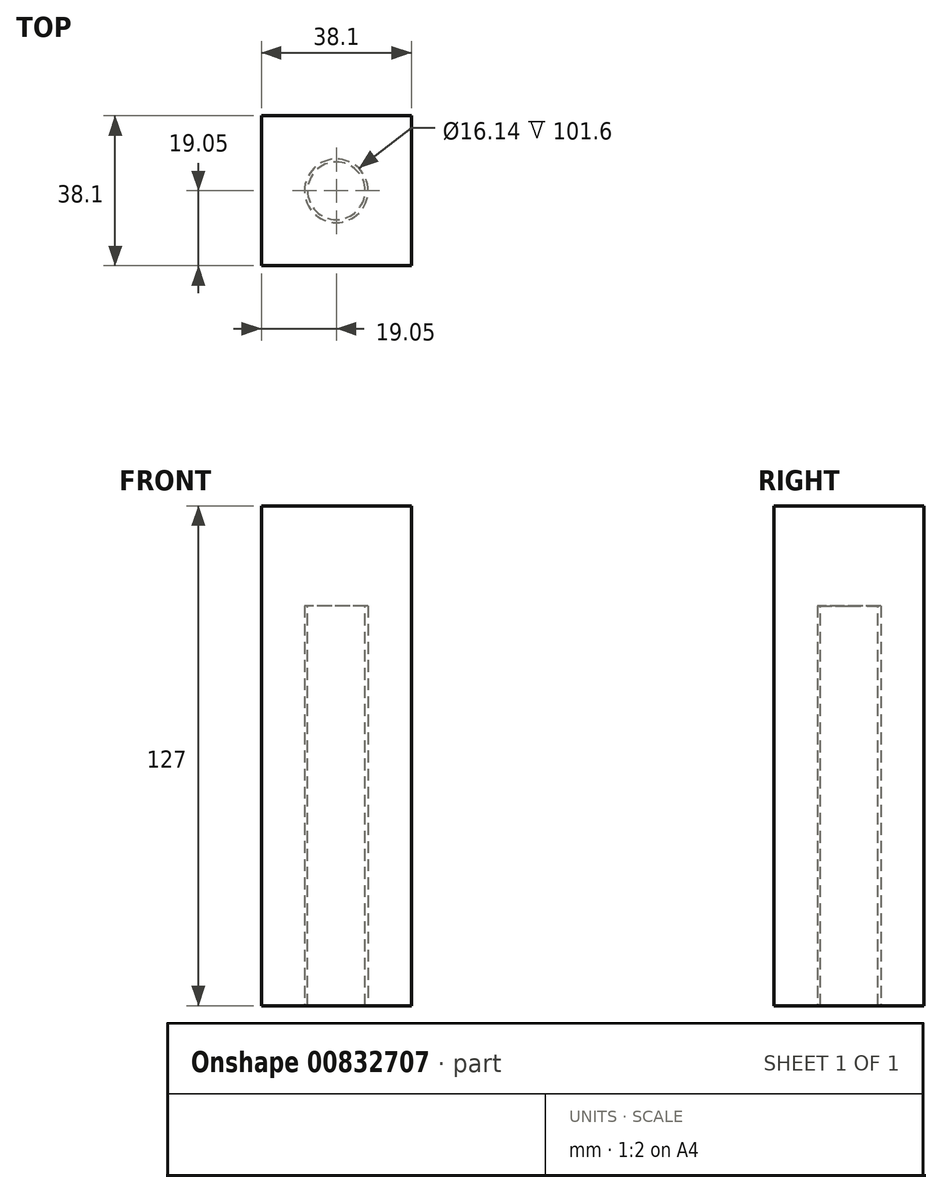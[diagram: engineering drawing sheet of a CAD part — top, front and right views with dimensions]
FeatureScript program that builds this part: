
annotation { "Feature Type Name" : "Feature", "Feature Type Description" : "" }
export const myFeature = defineFeature(function(context is Context, id is Id, definition is map)
    precondition{}
    {
        {
            var Q0;
            Q0=qCreatedBy(makeId("Top.planeOp"),FACE);
            var sketch = newSketch(context, id + "F0", { "sketchPlane" : qUnion([Q0])});
            skLineSegment(sketch, "E0", {"start": v(0, 0) * mm, "end": v(38.1, 0) * mm});
            skLineSegment(sketch, "E1", {"start": v(38.1, 0) * mm, "end": v(38.1, 38.1) * mm});
            skLineSegment(sketch, "E2", {"start": v(38.1, 38.1) * mm, "end": v(0, 38.1) * mm});
            skLineSegment(sketch, "E3", {"start": v(0, 38.1) * mm, "end": v(0, 0) * mm});
            skCircle(sketch, "E4", {"center": v(19.05, 19.05) * mm, "radius": 14.39 * mm});
            skPoint(sketch, "E4.centerSnap0", {"position": v(19.05, 38.1) * mm});
            skPoint(sketch, "E4.centerSnap1", {"position": v(0, 19.05) * mm});
            skCircle(sketch, "E5", {"center": v(19.05, 19.05) * mm, "radius": 8.07 * mm});
            skLineSegment(sketch, "E6", {"start": v(19.05, 0) * mm, "end": v(19.05, 38.1) * mm});
            skLineSegment(sketch, "E7", {"start": v(38.1, 19.05) * mm, "end": v(0, 19.05) * mm});
            skSolve(sketch);
        }
        {
            var Q0;
            {var subQ5=sQuery(id+"F0.wireOp",EDGE,"E2");var subQ7=sQuery(id+"F0.wireOp",EDGE,"E3");var subQ8=makeQuery(id+"F0.imprint","INTERSECT",VERTEX,{"derivedFrom":[subQ5,subQ7]});Q0=makeQuery(id+"F0.imprint","IMPRINT",FACE,{"disambiguationData":[TD([[makeQuery(id+"F0.imprint","IMPRINT",EDGE,{"disambiguationData":[TD([[subQ8,1.0]])],"derivedFrom":subQ5}),1.0]])]});}
            extrude(context, id + "F1", {"entities" : qUnion([Q0]), "depth" : 25.4 * mm, "offsetDistance" : 25.4 * mm});
        }
        {
            var Q0;
            {var subQ1=sQuery(id+"F0.wireOp",EDGE,"E2");var subQ5=sQuery(id+"F0.wireOp",EDGE,"E1");var subQ6=makeQuery(id+"F0.imprint","INTERSECT",VERTEX,{"derivedFrom":[subQ5,subQ1]});Q0=makeQuery(id+"F0.imprint","IMPRINT",FACE,{"disambiguationData":[TD([[makeQuery(id+"F0.imprint","IMPRINT",EDGE,{"disambiguationData":[TD([[subQ6,1.0]])],"derivedFrom":subQ5}),1.0]])]});}
            extrude(context, id + "F2", {"entities" : qUnion([Q0]), "operationType" : NewBodyOperationType.ADD, "depth" : 38.1 * mm, "offsetDistance" : 25.4 * mm});
        }
        {
            var Q0;
            {var subQ0=sQuery(id+"F0.wireOp",EDGE,"E1");var subQ1=sQuery(id+"F0.wireOp",EDGE,"E0");var subQ2=makeQuery(id+"F0.imprint","INTERSECT",VERTEX,{"derivedFrom":[subQ1,subQ0]});Q0=makeQuery(id+"F0.imprint","IMPRINT",FACE,{"disambiguationData":[TD([[makeQuery(id+"F0.imprint","IMPRINT",EDGE,{"disambiguationData":[TD([[subQ2,1.0]])],"derivedFrom":subQ1}),1.0]])]});}
            extrude(context, id + "F3", {"entities" : qUnion([Q0]), "operationType" : NewBodyOperationType.ADD, "depth" : 50.8 * mm, "offsetDistance" : 25.4 * mm});
        }
        {
            var Q0;
            {var subQ1=sQuery(id+"F0.wireOp",EDGE,"E0");var subQ6=sQuery(id+"F0.wireOp",EDGE,"E3");var subQ9=makeQuery(id+"F0.imprint","INTERSECT",VERTEX,{"derivedFrom":[subQ1,subQ6]});Q0=makeQuery(id+"F0.imprint","IMPRINT",FACE,{"disambiguationData":[TD([[makeQuery(id+"F0.imprint","IMPRINT",EDGE,{"disambiguationData":[TD([[subQ9,-1.0]])],"derivedFrom":subQ1}),1.0]])]});}
            extrude(context, id + "F4", {"entities" : qUnion([Q0]), "operationType" : NewBodyOperationType.ADD, "depth" : 63.5 * mm, "offsetDistance" : 25.4 * mm});
        }
        {
            var Q0;
            {var subQ0=sQuery(id+"F0.wireOp",EDGE,"E6");var subQ1=sQuery(id+"F0.wireOp",EDGE,"E4");var subQ2=makeQuery(id+"F0.imprint","INTERSECT",VERTEX,{"disambiguationData":[OD(0.0)],"derivedFrom":[subQ1,subQ0]});Q0=makeQuery(id+"F0.imprint","IMPRINT",FACE,{"disambiguationData":[TD([[makeQuery(id+"F0.imprint","IMPRINT",EDGE,{"disambiguationData":[TD([[subQ2,-1.0]])],"derivedFrom":subQ1}),1.0]])]});}
            var Q1;
            {var subQ0=sQuery(id+"F0.wireOp",EDGE,"E6");var subQ1=sQuery(id+"F0.wireOp",EDGE,"E4");var subQ2=makeQuery(id+"F0.imprint","INTERSECT",VERTEX,{"disambiguationData":[OD(0.0)],"derivedFrom":[subQ1,subQ0]});Q1=makeQuery(id+"F0.imprint","IMPRINT",FACE,{"disambiguationData":[TD([[makeQuery(id+"F0.imprint","IMPRINT",EDGE,{"disambiguationData":[TD([[subQ2,1.0]])],"derivedFrom":subQ1}),1.0]])]});}
            var Q2;
            {var subQ0=sQuery(id+"F0.wireOp",EDGE,"E7");var subQ1=sQuery(id+"F0.wireOp",EDGE,"E4");var subQ2=makeQuery(id+"F0.imprint","INTERSECT",VERTEX,{"disambiguationData":[OD(0.0)],"derivedFrom":[subQ1,subQ0]});Q2=makeQuery(id+"F0.imprint","IMPRINT",FACE,{"disambiguationData":[TD([[makeQuery(id+"F0.imprint","IMPRINT",EDGE,{"disambiguationData":[TD([[subQ2,1.0]])],"derivedFrom":subQ1}),1.0]])]});}
            var Q3;
            {var subQ0=sQuery(id+"F0.wireOp",EDGE,"E7");var subQ1=sQuery(id+"F0.wireOp",EDGE,"E4");var subQ2=makeQuery(id+"F0.imprint","INTERSECT",VERTEX,{"disambiguationData":[OD(1.0)],"derivedFrom":[subQ1,subQ0]});Q3=makeQuery(id+"F0.imprint","IMPRINT",FACE,{"disambiguationData":[TD([[makeQuery(id+"F0.imprint","IMPRINT",EDGE,{"disambiguationData":[TD([[subQ2,-1.0]])],"derivedFrom":subQ1}),1.0]])]});}
            extrude(context, id + "F5", {"entities" : qUnion([Q0, Q1, Q2, Q3]), "operationType" : NewBodyOperationType.ADD, "depth" : 101.6 * mm, "offsetDistance" : 25.4 * mm});
        }
        {
            var Q0;
            Q0=makeQuery(id+"F5.opExtrude","CAP_FACE",FACE,{"disambiguationData":[OSD([sQuery(id+"F0.wireOp",EDGE,"E4"),sQuery(id+"F0.wireOp",EDGE,"E5")])],"isStart":false});
            var sketch = newSketch(context, id + "F6", { "sketchPlane" : qUnion([Q0])});
            skCircle(sketch, "E8.0", {"center": v(19.05, 19.05) * mm, "radius": 14.39 * mm});
            skCircle(sketch, "E8.1", {"center": v(19.05, 19.05) * mm, "radius": 8.07 * mm});
            skPoint(sketch, "E8.2", {"position": v(19.05, 0) * mm});
            skPoint(sketch, "E8.3", {"position": v(19.05, 4.66) * mm});
            skPoint(sketch, "E8.4", {"position": v(0, 0) * mm});
            skPoint(sketch, "E8.5", {"position": v(0, 19.05) * mm});
            skPoint(sketch, "E8.6", {"position": v(4.66, 19.05) * mm});
            skPoint(sketch, "E8.7", {"position": v(0, 38.1) * mm});
            skPoint(sketch, "E8.8", {"position": v(19.05, 38.1) * mm});
            skPoint(sketch, "E8.9", {"position": v(38.1, 38.1) * mm});
            skPoint(sketch, "E8.10", {"position": v(38.1, 19.05) * mm});
            skPoint(sketch, "E8.11", {"position": v(38.1, 0) * mm});
            skLineSegment(sketch, "E9", {"start": v(0, 0) * mm, "end": v(0, 38.1) * mm});
            skLineSegment(sketch, "E10", {"start": v(38.1, 38.1) * mm, "end": v(0, 38.1) * mm});
            skLineSegment(sketch, "E11", {"start": v(38.1, 38.1) * mm, "end": v(38.1, 0) * mm});
            skLineSegment(sketch, "E12", {"start": v(38.1, 0) * mm, "end": v(0, 0) * mm});
            skLineSegment(sketch, "E13", {"start": v(19.05, 0) * mm, "end": v(19.05, 38.1) * mm});
            skLineSegment(sketch, "E14", {"start": v(38.1, 19.05) * mm, "end": v(0, 19.05) * mm});
            skCircle(sketch, "E15.0", {"center": v(19.05, 19.05) * mm, "radius": 7.3 * mm});
            skSolve(sketch);
        }
        {
            var Q0;
            {var subQ0=sQuery(id+"F6.wireOp",EDGE,"E14");var subQ1=sQuery(id+"F6.wireOp",EDGE,"E13");var subQ2=makeQuery(id+"F6.imprint","INTERSECT",VERTEX,{"derivedFrom":[subQ1,subQ0]});Q0=makeQuery(id+"F6.imprint","IMPRINT",FACE,{"disambiguationData":[TD([[makeQuery(id+"F6.imprint","IMPRINT",EDGE,{"disambiguationData":[TD([[subQ2,-1.0]])],"derivedFrom":subQ1}),1.0]])]});}
            var Q1;
            {var subQ0=sQuery(id+"F6.wireOp",EDGE,"E14");var subQ1=sQuery(id+"F6.wireOp",EDGE,"E13");var subQ2=makeQuery(id+"F6.imprint","INTERSECT",VERTEX,{"derivedFrom":[subQ1,subQ0]});Q1=makeQuery(id+"F6.imprint","IMPRINT",FACE,{"disambiguationData":[TD([[makeQuery(id+"F6.imprint","IMPRINT",EDGE,{"disambiguationData":[TD([[subQ2,-1.0]])],"derivedFrom":subQ1}),-1.0]])]});}
            var Q2;
            {var subQ0=sQuery(id+"F6.wireOp",EDGE,"E15.0");var subQ1=sQuery(id+"F6.wireOp",EDGE,"E13");var subQ2=makeQuery(id+"F6.imprint","INTERSECT",VERTEX,{"disambiguationData":[OD(0.0)],"derivedFrom":[subQ1,subQ0]});Q2=makeQuery(id+"F6.imprint","IMPRINT",FACE,{"disambiguationData":[TD([[makeQuery(id+"F6.imprint","IMPRINT",EDGE,{"disambiguationData":[TD([[subQ2,-1.0]])],"derivedFrom":subQ1}),1.0]])]});}
            var Q3;
            {var subQ0=sQuery(id+"F6.wireOp",EDGE,"E15.0");var subQ1=sQuery(id+"F6.wireOp",EDGE,"E13");var subQ2=makeQuery(id+"F6.imprint","INTERSECT",VERTEX,{"disambiguationData":[OD(0.0)],"derivedFrom":[subQ1,subQ0]});Q3=makeQuery(id+"F6.imprint","IMPRINT",FACE,{"disambiguationData":[TD([[makeQuery(id+"F6.imprint","IMPRINT",EDGE,{"disambiguationData":[TD([[subQ2,-1.0]])],"derivedFrom":subQ1}),-1.0]])]});}
            var Q4;
            {var subQ0=sQuery(id+"F0.wireOp",EDGE,"E4");var subQ1=sQuery(id+"F0.wireOp",EDGE,"E7");var subQ2=sQuery(id+"F0.wireOp",EDGE,"E6");var subQ3=sQuery(id+"F0.wireOp",EDGE,"E3");var subQ4=sQuery(id+"F0.wireOp",EDGE,"E0");var subQ5=sQuery(id+"F0.wireOp",EDGE,"E1");var subQ6=sQuery(id+"F0.wireOp",EDGE,"E2");Q4=makeQuery(id+"F5.boolean.opBoolean","MERGE",FACE,{"derivedFrom":[makeQuery(id+"F4.boolean.opBoolean","MERGE",FACE,{"derivedFrom":[makeQuery(id+"F3.boolean.opBoolean","MERGE",FACE,{"derivedFrom":[makeQuery(id+"F2.boolean.opBoolean","MERGE",FACE,{"derivedFrom":[makeQuery(id+"F1.opExtrude","CAP_FACE",FACE,{"disambiguationData":[OSD([subQ6,subQ3,subQ0,subQ2,subQ1])],"isStart":true}),makeQuery(id+"F2.opExtrude","CAP_FACE",FACE,{"disambiguationData":[OSD([subQ5,subQ6,subQ0,subQ2,subQ1])],"isStart":true})]}),makeQuery(id+"F3.opExtrude","CAP_FACE",FACE,{"disambiguationData":[OSD([subQ4,subQ5,subQ0,subQ2,subQ1])],"isStart":true})]}),makeQuery(id+"F4.opExtrude","CAP_FACE",FACE,{"disambiguationData":[OSD([subQ4,subQ3,subQ0,subQ2,subQ1])],"isStart":true})]}),makeQuery(id+"F5.opExtrude","CAP_FACE",FACE,{"disambiguationData":[OSD([subQ0,sQuery(id+"F0.wireOp",EDGE,"E5")])],"isStart":true})]});}
            extrude(context, id + "F7", {"entities" : qUnion([Q0, Q1, Q2, Q3]), "endBound" : BoundingType.UP_TO_SURFACE, "oppositeDirection" : true, "depth" : 25.4 * mm, "endBoundEntityFace" : qUnion([Q4]), "offsetDistance" : 25.4 * mm});
        }
        {
            var Q0;
            {var subQ3=sQuery(id+"F6.wireOp",EDGE,"E8.0");var subQ7=sQuery(id+"F6.wireOp",EDGE,"E14");var subQ8=makeQuery(id+"F6.imprint","INTERSECT",VERTEX,{"disambiguationData":[OD(0.0)],"derivedFrom":[subQ3,subQ7]});Q0=makeQuery(id+"F6.imprint","IMPRINT",FACE,{"disambiguationData":[TD([[makeQuery(id+"F6.imprint","IMPRINT",EDGE,{"disambiguationData":[TD([[subQ8,1.0]])],"derivedFrom":subQ3}),-1.0]])]});}
            var Q1;
            {var subQ0=sQuery(id+"F6.wireOp",EDGE,"E14");var subQ1=sQuery(id+"F6.wireOp",EDGE,"E8.0");var subQ2=makeQuery(id+"F6.imprint","INTERSECT",VERTEX,{"disambiguationData":[OD(0.0)],"derivedFrom":[subQ1,subQ0]});Q1=makeQuery(id+"F6.imprint","IMPRINT",FACE,{"disambiguationData":[TD([[makeQuery(id+"F6.imprint","IMPRINT",EDGE,{"disambiguationData":[TD([[subQ2,1.0]])],"derivedFrom":subQ1}),1.0]])]});}
            var Q2;
            {var subQ0=sQuery(id+"F6.wireOp",EDGE,"E14");var subQ1=sQuery(id+"F6.wireOp",EDGE,"E8.1");var subQ2=makeQuery(id+"F6.imprint","INTERSECT",VERTEX,{"disambiguationData":[OD(0.0)],"derivedFrom":[subQ1,subQ0]});Q2=makeQuery(id+"F6.imprint","IMPRINT",FACE,{"disambiguationData":[TD([[makeQuery(id+"F6.imprint","IMPRINT",EDGE,{"disambiguationData":[TD([[subQ2,1.0]])],"derivedFrom":subQ1}),1.0]])]});}
            var Q3;
            {var subQ0=sQuery(id+"F6.wireOp",EDGE,"E15.0");var subQ1=sQuery(id+"F6.wireOp",EDGE,"E13");var subQ2=makeQuery(id+"F6.imprint","INTERSECT",VERTEX,{"disambiguationData":[OD(0.0)],"derivedFrom":[subQ1,subQ0]});Q3=makeQuery(id+"F6.imprint","IMPRINT",FACE,{"disambiguationData":[TD([[makeQuery(id+"F6.imprint","IMPRINT",EDGE,{"disambiguationData":[TD([[subQ2,-1.0]])],"derivedFrom":subQ1}),-1.0]])]});}
            var Q4;
            {var subQ0=sQuery(id+"F6.wireOp",EDGE,"E15.0");var subQ1=sQuery(id+"F6.wireOp",EDGE,"E13");var subQ2=makeQuery(id+"F6.imprint","INTERSECT",VERTEX,{"disambiguationData":[OD(0.0)],"derivedFrom":[subQ1,subQ0]});Q4=makeQuery(id+"F6.imprint","IMPRINT",FACE,{"disambiguationData":[TD([[makeQuery(id+"F6.imprint","IMPRINT",EDGE,{"disambiguationData":[TD([[subQ2,-1.0]])],"derivedFrom":subQ1}),1.0]])]});}
            var Q5;
            {var subQ0=sQuery(id+"F6.wireOp",EDGE,"E14");var subQ1=sQuery(id+"F6.wireOp",EDGE,"E8.1");var subQ2=makeQuery(id+"F6.imprint","INTERSECT",VERTEX,{"disambiguationData":[OD(1.0)],"derivedFrom":[subQ1,subQ0]});Q5=makeQuery(id+"F6.imprint","IMPRINT",FACE,{"disambiguationData":[TD([[makeQuery(id+"F6.imprint","IMPRINT",EDGE,{"disambiguationData":[TD([[subQ2,-1.0]])],"derivedFrom":subQ1}),1.0]])]});}
            var Q6;
            {var subQ0=sQuery(id+"F6.wireOp",EDGE,"E14");var subQ1=sQuery(id+"F6.wireOp",EDGE,"E8.0");var subQ2=makeQuery(id+"F6.imprint","INTERSECT",VERTEX,{"disambiguationData":[OD(1.0)],"derivedFrom":[subQ1,subQ0]});Q6=makeQuery(id+"F6.imprint","IMPRINT",FACE,{"disambiguationData":[TD([[makeQuery(id+"F6.imprint","IMPRINT",EDGE,{"disambiguationData":[TD([[subQ2,-1.0]])],"derivedFrom":subQ1}),1.0]])]});}
            var Q7;
            {var subQ3=sQuery(id+"F6.wireOp",EDGE,"E8.0");var subQ7=sQuery(id+"F6.wireOp",EDGE,"E14");var subQ9=makeQuery(id+"F6.imprint","INTERSECT",VERTEX,{"disambiguationData":[OD(1.0)],"derivedFrom":[subQ3,subQ7]});Q7=makeQuery(id+"F6.imprint","IMPRINT",FACE,{"disambiguationData":[TD([[makeQuery(id+"F6.imprint","IMPRINT",EDGE,{"disambiguationData":[TD([[subQ9,-1.0]])],"derivedFrom":subQ3}),-1.0]])]});}
            var Q8;
            {var subQ0=sQuery(id+"F6.wireOp",EDGE,"E14");var subQ1=sQuery(id+"F6.wireOp",EDGE,"E13");var subQ2=makeQuery(id+"F6.imprint","INTERSECT",VERTEX,{"derivedFrom":[subQ1,subQ0]});Q8=makeQuery(id+"F6.imprint","IMPRINT",FACE,{"disambiguationData":[TD([[makeQuery(id+"F6.imprint","IMPRINT",EDGE,{"disambiguationData":[TD([[subQ2,-1.0]])],"derivedFrom":subQ1}),1.0]])]});}
            var Q9;
            {var subQ0=sQuery(id+"F6.wireOp",EDGE,"E13");var subQ1=sQuery(id+"F6.wireOp",EDGE,"E8.1");var subQ2=makeQuery(id+"F6.imprint","INTERSECT",VERTEX,{"disambiguationData":[OD(0.0)],"derivedFrom":[subQ1,subQ0]});Q9=makeQuery(id+"F6.imprint","IMPRINT",FACE,{"disambiguationData":[TD([[makeQuery(id+"F6.imprint","IMPRINT",EDGE,{"disambiguationData":[TD([[subQ2,-1.0]])],"derivedFrom":subQ1}),1.0]])]});}
            var Q10;
            {var subQ0=sQuery(id+"F6.wireOp",EDGE,"E13");var subQ1=sQuery(id+"F6.wireOp",EDGE,"E8.0");var subQ2=makeQuery(id+"F6.imprint","INTERSECT",VERTEX,{"disambiguationData":[OD(0.0)],"derivedFrom":[subQ1,subQ0]});Q10=makeQuery(id+"F6.imprint","IMPRINT",FACE,{"disambiguationData":[TD([[makeQuery(id+"F6.imprint","IMPRINT",EDGE,{"disambiguationData":[TD([[subQ2,-1.0]])],"derivedFrom":subQ1}),1.0]])]});}
            var Q11;
            {var subQ0=sQuery(id+"F6.wireOp",EDGE,"E13");var subQ3=sQuery(id+"F6.wireOp",EDGE,"E8.0");var subQ4=makeQuery(id+"F6.imprint","INTERSECT",VERTEX,{"disambiguationData":[OD(0.0)],"derivedFrom":[subQ3,subQ0]});Q11=makeQuery(id+"F6.imprint","IMPRINT",FACE,{"disambiguationData":[TD([[makeQuery(id+"F6.imprint","IMPRINT",EDGE,{"disambiguationData":[TD([[subQ4,-1.0]])],"derivedFrom":subQ3}),-1.0]])]});}
            var Q12;
            {var subQ0=sQuery(id+"F6.wireOp",EDGE,"E14");var subQ1=sQuery(id+"F6.wireOp",EDGE,"E13");var subQ2=makeQuery(id+"F6.imprint","INTERSECT",VERTEX,{"derivedFrom":[subQ1,subQ0]});Q12=makeQuery(id+"F6.imprint","IMPRINT",FACE,{"disambiguationData":[TD([[makeQuery(id+"F6.imprint","IMPRINT",EDGE,{"disambiguationData":[TD([[subQ2,-1.0]])],"derivedFrom":subQ1}),-1.0]])]});}
            var Q13;
            {var subQ0=sQuery(id+"F6.wireOp",EDGE,"E13");var subQ1=sQuery(id+"F6.wireOp",EDGE,"E8.1");var subQ2=makeQuery(id+"F6.imprint","INTERSECT",VERTEX,{"disambiguationData":[OD(0.0)],"derivedFrom":[subQ1,subQ0]});Q13=makeQuery(id+"F6.imprint","IMPRINT",FACE,{"disambiguationData":[TD([[makeQuery(id+"F6.imprint","IMPRINT",EDGE,{"disambiguationData":[TD([[subQ2,1.0]])],"derivedFrom":subQ1}),1.0]])]});}
            var Q14;
            {var subQ0=sQuery(id+"F6.wireOp",EDGE,"E13");var subQ1=sQuery(id+"F6.wireOp",EDGE,"E8.0");var subQ2=makeQuery(id+"F6.imprint","INTERSECT",VERTEX,{"disambiguationData":[OD(0.0)],"derivedFrom":[subQ1,subQ0]});Q14=makeQuery(id+"F6.imprint","IMPRINT",FACE,{"disambiguationData":[TD([[makeQuery(id+"F6.imprint","IMPRINT",EDGE,{"disambiguationData":[TD([[subQ2,1.0]])],"derivedFrom":subQ1}),1.0]])]});}
            var Q15;
            {var subQ0=sQuery(id+"F6.wireOp",EDGE,"E13");var subQ3=sQuery(id+"F6.wireOp",EDGE,"E8.0");var subQ4=makeQuery(id+"F6.imprint","INTERSECT",VERTEX,{"disambiguationData":[OD(0.0)],"derivedFrom":[subQ3,subQ0]});Q15=makeQuery(id+"F6.imprint","IMPRINT",FACE,{"disambiguationData":[TD([[makeQuery(id+"F6.imprint","IMPRINT",EDGE,{"disambiguationData":[TD([[subQ4,1.0]])],"derivedFrom":subQ3}),-1.0]])]});}
            extrude(context, id + "F8", {"entities" : qUnion([Q0, Q1, Q2, Q3, Q4, Q5, Q6, Q7, Q8, Q9, Q10, Q11, Q12, Q13, Q14, Q15]), "operationType" : NewBodyOperationType.ADD, "depth" : 25.4 * mm, "offsetDistance" : 25.4 * mm});
        }
        {
            var Q0;
            {var subQ3=sQuery(id+"F6.wireOp",EDGE,"E8.0");var subQ7=sQuery(id+"F6.wireOp",EDGE,"E14");var subQ9=makeQuery(id+"F6.imprint","INTERSECT",VERTEX,{"disambiguationData":[OD(1.0)],"derivedFrom":[subQ3,subQ7]});Q0=makeQuery(id+"F6.imprint","IMPRINT",FACE,{"disambiguationData":[TD([[makeQuery(id+"F6.imprint","IMPRINT",EDGE,{"disambiguationData":[TD([[subQ9,-1.0]])],"derivedFrom":subQ3}),-1.0]])]});}
            extrude(context, id + "F9", {"entities" : qUnion([Q0]), "operationType" : NewBodyOperationType.ADD, "endBound" : BoundingType.UP_TO_NEXT, "oppositeDirection" : true, "depth" : 25.4 * mm, "offsetDistance" : 25.4 * mm});
        }
        {
            var Q0;
            {var subQ3=sQuery(id+"F6.wireOp",EDGE,"E8.0");var subQ7=sQuery(id+"F6.wireOp",EDGE,"E14");var subQ8=makeQuery(id+"F6.imprint","INTERSECT",VERTEX,{"disambiguationData":[OD(0.0)],"derivedFrom":[subQ3,subQ7]});Q0=makeQuery(id+"F6.imprint","IMPRINT",FACE,{"disambiguationData":[TD([[makeQuery(id+"F6.imprint","IMPRINT",EDGE,{"disambiguationData":[TD([[subQ8,1.0]])],"derivedFrom":subQ3}),-1.0]])]});}
            extrude(context, id + "F10", {"entities" : qUnion([Q0]), "operationType" : NewBodyOperationType.ADD, "endBound" : BoundingType.UP_TO_NEXT, "oppositeDirection" : true, "depth" : 25.4 * mm, "offsetDistance" : 25.4 * mm});
        }
        {
            var Q0;
            {var subQ0=sQuery(id+"F6.wireOp",EDGE,"E13");var subQ3=sQuery(id+"F6.wireOp",EDGE,"E8.0");var subQ4=makeQuery(id+"F6.imprint","INTERSECT",VERTEX,{"disambiguationData":[OD(0.0)],"derivedFrom":[subQ3,subQ0]});Q0=makeQuery(id+"F6.imprint","IMPRINT",FACE,{"disambiguationData":[TD([[makeQuery(id+"F6.imprint","IMPRINT",EDGE,{"disambiguationData":[TD([[subQ4,1.0]])],"derivedFrom":subQ3}),-1.0]])]});}
            extrude(context, id + "F11", {"entities" : qUnion([Q0]), "operationType" : NewBodyOperationType.ADD, "endBound" : BoundingType.UP_TO_NEXT, "oppositeDirection" : true, "depth" : 25.4 * mm, "offsetDistance" : 25.4 * mm});
        }
        {
            var Q0;
            {var subQ0=sQuery(id+"F6.wireOp",EDGE,"E13");var subQ3=sQuery(id+"F6.wireOp",EDGE,"E8.0");var subQ4=makeQuery(id+"F6.imprint","INTERSECT",VERTEX,{"disambiguationData":[OD(0.0)],"derivedFrom":[subQ3,subQ0]});Q0=makeQuery(id+"F6.imprint","IMPRINT",FACE,{"disambiguationData":[TD([[makeQuery(id+"F6.imprint","IMPRINT",EDGE,{"disambiguationData":[TD([[subQ4,-1.0]])],"derivedFrom":subQ3}),-1.0]])]});}
            extrude(context, id + "F12", {"entities" : qUnion([Q0]), "operationType" : NewBodyOperationType.ADD, "endBound" : BoundingType.UP_TO_NEXT, "oppositeDirection" : true, "depth" : 25.4 * mm, "offsetDistance" : 25.4 * mm});
        }
    });
